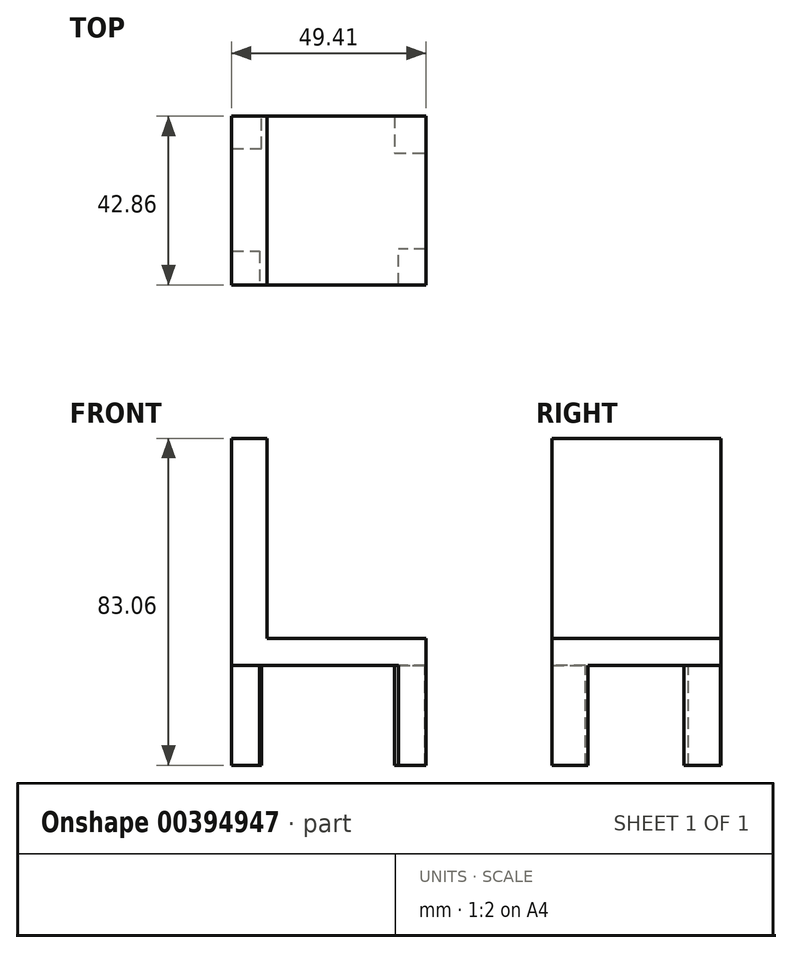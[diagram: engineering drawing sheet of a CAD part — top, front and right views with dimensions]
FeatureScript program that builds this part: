
annotation { "Feature Type Name" : "Feature", "Feature Type Description" : "" }
export const myFeature = defineFeature(function(context is Context, id is Id, definition is map)
    precondition{}
    {
        {
            var Q0;
            Q0=qCreatedBy(makeId("Top.planeOp"),FACE);
            var sketch = newSketch(context, id + "F0", { "sketchPlane" : qUnion([Q0])});
            skLineSegment(sketch, "E0.bottom", {"start": v(-9.55, -3) * mm, "end": v(39.86, -3) * mm});
            skLineSegment(sketch, "E0.top", {"start": v(-9.55, 39.85) * mm, "end": v(39.86, 39.85) * mm});
            skLineSegment(sketch, "E0.left", {"start": v(-9.55, -3) * mm, "end": v(-9.55, 39.85) * mm});
            skLineSegment(sketch, "E0.right", {"start": v(39.86, -3) * mm, "end": v(39.86, 39.85) * mm});
            skSolve(sketch);
        }
        {
            var Q0;
            Q0=makeQuery(id+"F0.imprint","IMPRINT",FACE,{"disambiguationData":[TD([[makeQuery(id+"F0.imprint","IMPRINT",EDGE,{"derivedFrom":sQuery(id+"F0.wireOp",EDGE,"E0.bottom")}),1.0]])]});
            extrude(context, id + "F1", {"entities" : qUnion([Q0]), "depth" : 6.86 * mm});
        }
        {
            var Q0;
            Q0=makeQuery(id+"F1.opExtrude","CAP_FACE",FACE,{"disambiguationData":[OSD([sQuery(id+"F0.wireOp",EDGE,"E0.bottom"),sQuery(id+"F0.wireOp",EDGE,"E0.top"),sQuery(id+"F0.wireOp",EDGE,"E0.left"),sQuery(id+"F0.wireOp",EDGE,"E0.right")])],"isStart":true});
            var sketch = newSketch(context, id + "F2", { "sketchPlane" : qUnion([Q0])});
            skLineSegment(sketch, "E1.bottom", {"start": v(39.86, 3) * mm, "end": v(32.85, 3) * mm});
            skLineSegment(sketch, "E1.top", {"start": v(39.86, -6.14) * mm, "end": v(32.85, -6.14) * mm});
            skLineSegment(sketch, "E1.left", {"start": v(39.86, 3) * mm, "end": v(39.86, -6.14) * mm});
            skLineSegment(sketch, "E1.right", {"start": v(32.85, 3) * mm, "end": v(32.85, -6.14) * mm});
            skSolve(sketch);
        }
        {
            var Q0;
            {var subQ4=sQuery(id+"F2.wireOp",EDGE,"E1.top");Q0=makeQuery(id+"F2.imprint","IMPRINT",FACE,{"disambiguationData":[TD([[makeQuery(id+"F2.imprint","IMPRINT",EDGE,{"derivedFrom":subQ4}),1.0]])]});}
            var sketch = newSketch(context, id + "F3", { "sketchPlane" : qUnion([Q0])});
            skLineSegment(sketch, "E2.bottom", {"start": v(-9.48, -5.55) * mm, "end": v(-2.44, -5.55) * mm});
            skLineSegment(sketch, "E2.top", {"start": v(-9.48, 2.84) * mm, "end": v(-2.44, 2.84) * mm});
            skLineSegment(sketch, "E2.left", {"start": v(-9.48, -5.55) * mm, "end": v(-9.48, 2.84) * mm});
            skLineSegment(sketch, "E2.right", {"start": v(-2.44, -5.55) * mm, "end": v(-2.44, 2.84) * mm});
            skLineSegment(sketch, "E3.bottom", {"start": v(-9.48, -31.63) * mm, "end": v(-1.94, -31.63) * mm});
            skLineSegment(sketch, "E3.top", {"start": v(-9.48, -39.9) * mm, "end": v(-1.94, -39.9) * mm});
            skLineSegment(sketch, "E3.left", {"start": v(-9.48, -31.63) * mm, "end": v(-9.48, -39.9) * mm});
            skLineSegment(sketch, "E3.right", {"start": v(-1.94, -31.63) * mm, "end": v(-1.94, -39.9) * mm});
            skLineSegment(sketch, "E4.bottom", {"start": v(31.8, -39.8) * mm, "end": v(39.63, -39.8) * mm});
            skLineSegment(sketch, "E4.top", {"start": v(31.8, -30.5) * mm, "end": v(39.63, -30.5) * mm});
            skLineSegment(sketch, "E4.left", {"start": v(31.8, -39.8) * mm, "end": v(31.8, -30.5) * mm});
            skLineSegment(sketch, "E4.right", {"start": v(39.63, -39.8) * mm, "end": v(39.63, -30.5) * mm});
            skSolve(sketch);
        }
        {
            var Q0;
            Q0=makeQuery(id+"F3.imprint","IMPRINT",FACE,{"disambiguationData":[TD([[makeQuery(id+"F3.imprint","IMPRINT",EDGE,{"derivedFrom":sQuery(id+"F3.wireOp",EDGE,"E4.bottom")}),1.0]])]});
            var Q1;
            Q1=makeQuery(id+"F2.imprint","IMPRINT",FACE,{"disambiguationData":[TD([[makeQuery(id+"F2.imprint","IMPRINT",EDGE,{"derivedFrom":sQuery(id+"F2.wireOp",EDGE,"E1.bottom")}),-1.0]])]});
            var Q2;
            {var subQ0=sQuery(id+"F3.wireOp",EDGE,"E3.bottom");Q2=makeQuery(id+"F3.imprint","IMPRINT",FACE,{"disambiguationData":[TD([[makeQuery(id+"F3.imprint","IMPRINT",EDGE,{"derivedFrom":subQ0}),-1.0]])]});}
            var Q3;
            Q3=makeQuery(id+"F3.imprint","IMPRINT",FACE,{"disambiguationData":[TD([[makeQuery(id+"F3.imprint","IMPRINT",EDGE,{"derivedFrom":sQuery(id+"F3.wireOp",EDGE,"E2.bottom")}),1.0]])]});
            extrude(context, id + "F4", {"entities" : qUnion([Q0, Q1, Q2, Q3]), "operationType" : NewBodyOperationType.ADD, "depth" : 25.4 * mm});
        }
        {
            var Q0;
            Q0=makeQuery(id+"F1.opExtrude","CAP_FACE",FACE,{"disambiguationData":[OSD([sQuery(id+"F0.wireOp",EDGE,"E0.bottom"),sQuery(id+"F0.wireOp",EDGE,"E0.top"),sQuery(id+"F0.wireOp",EDGE,"E0.left"),sQuery(id+"F0.wireOp",EDGE,"E0.right")])],"isStart":false});
            var sketch = newSketch(context, id + "F5", { "sketchPlane" : qUnion([Q0])});
            skLineSegment(sketch, "E5.bottom", {"start": v(-9.55, 39.85) * mm, "end": v(-0.56, 39.85) * mm});
            skLineSegment(sketch, "E5.top", {"start": v(-9.55, -3) * mm, "end": v(-0.56, -3) * mm});
            skLineSegment(sketch, "E5.left", {"start": v(-9.55, 39.85) * mm, "end": v(-9.55, -3) * mm});
            skLineSegment(sketch, "E5.right", {"start": v(-0.56, 39.85) * mm, "end": v(-0.56, -3) * mm});
            skSolve(sketch);
        }
        {
            var Q0;
            Q0=makeQuery(id+"F5.imprint","IMPRINT",FACE,{"disambiguationData":[TD([[makeQuery(id+"F5.imprint","IMPRINT",EDGE,{"derivedFrom":sQuery(id+"F5.wireOp",EDGE,"E5.bottom")}),-1.0]])]});
            extrude(context, id + "F6", {"entities" : qUnion([Q0]), "operationType" : NewBodyOperationType.ADD, "depth" : 50.8 * mm});
        }
    });
